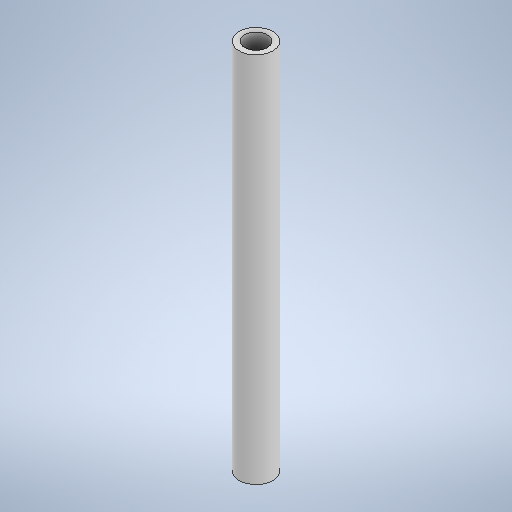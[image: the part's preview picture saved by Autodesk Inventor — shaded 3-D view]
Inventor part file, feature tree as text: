
AUTODESK INVENTOR PART (.ipt)
format: ipt  version: 2025.1 (Build 291241000, 241)  size: 250,368 bytes
history: native  units: mm
features: extrude x1, sketch x1
ambient origin geometry x8: Origin, YZ Plane, XZ Plane, XY Plane, X Axis, Y Axis, Z Axis, Center Point
bodies: Solid1 (feature_tree)
feature tree (2):
  extrude  "Extrusion1"  Depth=66.0mm
  sketch  "Sketch1"  dims[d0=6.0mm d1=4.0mm d2=66.0mm d3=0.0mm]
